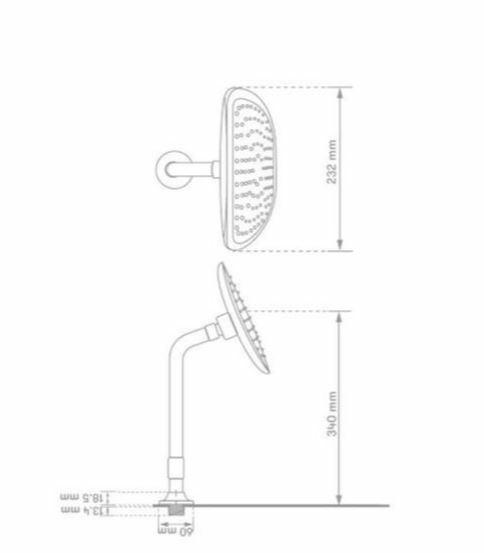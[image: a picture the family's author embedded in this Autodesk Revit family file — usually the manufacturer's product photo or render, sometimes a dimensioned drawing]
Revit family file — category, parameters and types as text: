
# Revit family: 01-1734-11 CONJUNTO REGISTRO DUCHA HELIX PALA
name_source: partatom
category: Plumbing Fixtures
revit_build: Autodesk Revit 2018 (Build: 20170223_1515(x64)
units: mm (PartAtom-declared; Revit-internal decimal feet)

## family parameters
Cut with Voids When Loaded = No
Host = Face
OmniClass Number = 23.31.11.00
Part Type = Normal
Room Calculation Point = No
Round Connector Dimension = Use Diameter
Shared = No

## types (1)
- 01-1734-11
    Alto manija = 85 mm  [stored 0.278871 ft]
    Ancho manija = 67 mm
    CW Connection = Yes
    Default Elevation = 0 mm  [stored 0 ft]
    Description = Mezclador ducha
    Escudo = 60 mm  [stored 0.19685 ft]
    HW Connection = Yes
    Laton = Laton
    Link Ficha Tecnica = No encontrada en internet
    Manufacturer = Gricol
    Model = 01-1734-11
    Plastico - ABS Cromado = Plastico ABS Cromado
    Product Name = CONJUNTO REGISTRO DUCHA HELIX PALA
    Sepacion entre registro y ducha = 400 mm  [stored 1.31234 ft]
    Type Image = <None>
    URL = https://www.gricol.com
    Vent Connection = No
    Waste Connection = No

note: [stored X ft] marks values corroborated as IEEE doubles in the binary element streams (Revit-internal decimal feet)

## geometry (parser evidence)
native form markers: Blend x4, Sweep x19
no freeform markers — native parametric forms only
